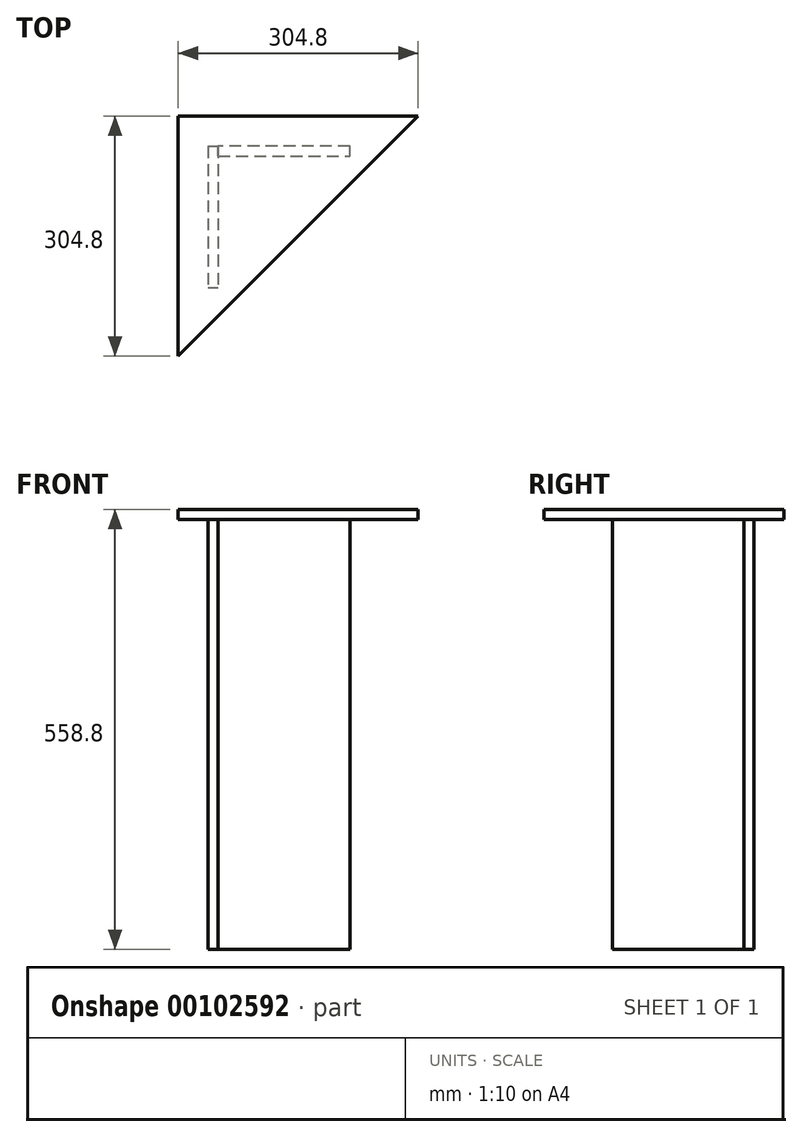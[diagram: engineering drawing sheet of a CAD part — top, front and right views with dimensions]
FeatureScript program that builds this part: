
annotation { "Feature Type Name" : "Feature", "Feature Type Description" : "" }
export const myFeature = defineFeature(function(context is Context, id is Id, definition is map)
    precondition{}
    {
        {
            var Q0;
            Q0=qCreatedBy(makeId("Top.planeOp"),FACE);
            var sketch = newSketch(context, id + "F0", { "sketchPlane" : qUnion([Q0])});
            skLineSegment(sketch, "E0", {"start": v(152.4, 152.4) * mm, "end": v(-152.4, 152.4) * mm});
            skLineSegment(sketch, "E1", {"start": v(-152.4, 152.4) * mm, "end": v(-152.4, -152.4) * mm});
            skLineSegment(sketch, "E2", {"start": v(-152.4, -152.4) * mm, "end": v(152.4, 152.4) * mm});
            skLineSegment(sketch, "E3.bottom", {"start": v(-114.3, 114.3) * mm, "end": v(-101.6, 114.3) * mm});
            skLineSegment(sketch, "E3.top", {"start": v(-114.3, -65.68) * mm, "end": v(-101.6, -65.68) * mm});
            skLineSegment(sketch, "E3.left", {"start": v(-114.3, 114.3) * mm, "end": v(-114.3, -65.68) * mm});
            skLineSegment(sketch, "E3.right", {"start": v(-101.6, 114.3) * mm, "end": v(-101.6, -65.68) * mm});
            skLineSegment(sketch, "E4", {"start": v(-101.6, 114.3) * mm, "end": v(65.68, 114.3) * mm});
            skLineSegment(sketch, "E5", {"start": v(65.68, 114.3) * mm, "end": v(65.68, 101.6) * mm});
            skLineSegment(sketch, "E6", {"start": v(65.68, 101.6) * mm, "end": v(-101.6, 101.6) * mm});
            skSolve(sketch);
        }
        {
            var Q0;
            Q0=makeQuery(id+"F0.imprint","IMPRINT",FACE,{"disambiguationData":[TD([[makeQuery(id+"F0.imprint","IMPRINT",EDGE,{"derivedFrom":sQuery(id+"F0.wireOp",EDGE,"E0")}),1.0]])]});
            var Q1;
            {var subQ1=sQuery(id+"F0.wireOp",EDGE,"E3.bottom");Q1=makeQuery(id+"F0.imprint","IMPRINT",FACE,{"disambiguationData":[TD([[makeQuery(id+"F0.imprint","IMPRINT",EDGE,{"derivedFrom":subQ1}),-1.0]])]});}
            var Q2;
            {var subQ0=sQuery(id+"F0.wireOp",EDGE,"E4");Q2=makeQuery(id+"F0.imprint","IMPRINT",FACE,{"disambiguationData":[TD([[makeQuery(id+"F0.imprint","IMPRINT",EDGE,{"derivedFrom":subQ0}),-1.0]])]});}
            extrude(context, id + "F1", {"entities" : qUnion([Q0, Q1, Q2]), "depth" : 12.7 * mm});
        }
        {
            var Q0;
            {var subQ1=sQuery(id+"F0.wireOp",EDGE,"E3.bottom");Q0=makeQuery(id+"F0.imprint","IMPRINT",FACE,{"disambiguationData":[TD([[makeQuery(id+"F0.imprint","IMPRINT",EDGE,{"derivedFrom":subQ1}),-1.0]])]});}
            extrude(context, id + "F2", {"entities" : qUnion([Q0]), "oppositeDirection" : true, "depth" : 546.1 * mm});
        }
        {
            var Q0;
            {var subQ0=sQuery(id+"F0.wireOp",EDGE,"E4");Q0=makeQuery(id+"F0.imprint","IMPRINT",FACE,{"disambiguationData":[TD([[makeQuery(id+"F0.imprint","IMPRINT",EDGE,{"derivedFrom":subQ0}),-1.0]])]});}
            var Q1;
            Q1=makeQuery(id+"F2.opExtrude","CAP_FACE",FACE,{"disambiguationData":[OSD([sQuery(id+"F0.wireOp",EDGE,"E3.bottom"),sQuery(id+"F0.wireOp",EDGE,"E3.top"),sQuery(id+"F0.wireOp",EDGE,"E3.left"),sQuery(id+"F0.wireOp",EDGE,"E3.right")])],"isStart":false});
            extrude(context, id + "F3", {"entities" : qUnion([Q0]), "endBound" : BoundingType.UP_TO_SURFACE, "oppositeDirection" : true, "endBoundEntityFace" : qUnion([Q1]), "depth" : 25.4 * mm});
        }
    });
